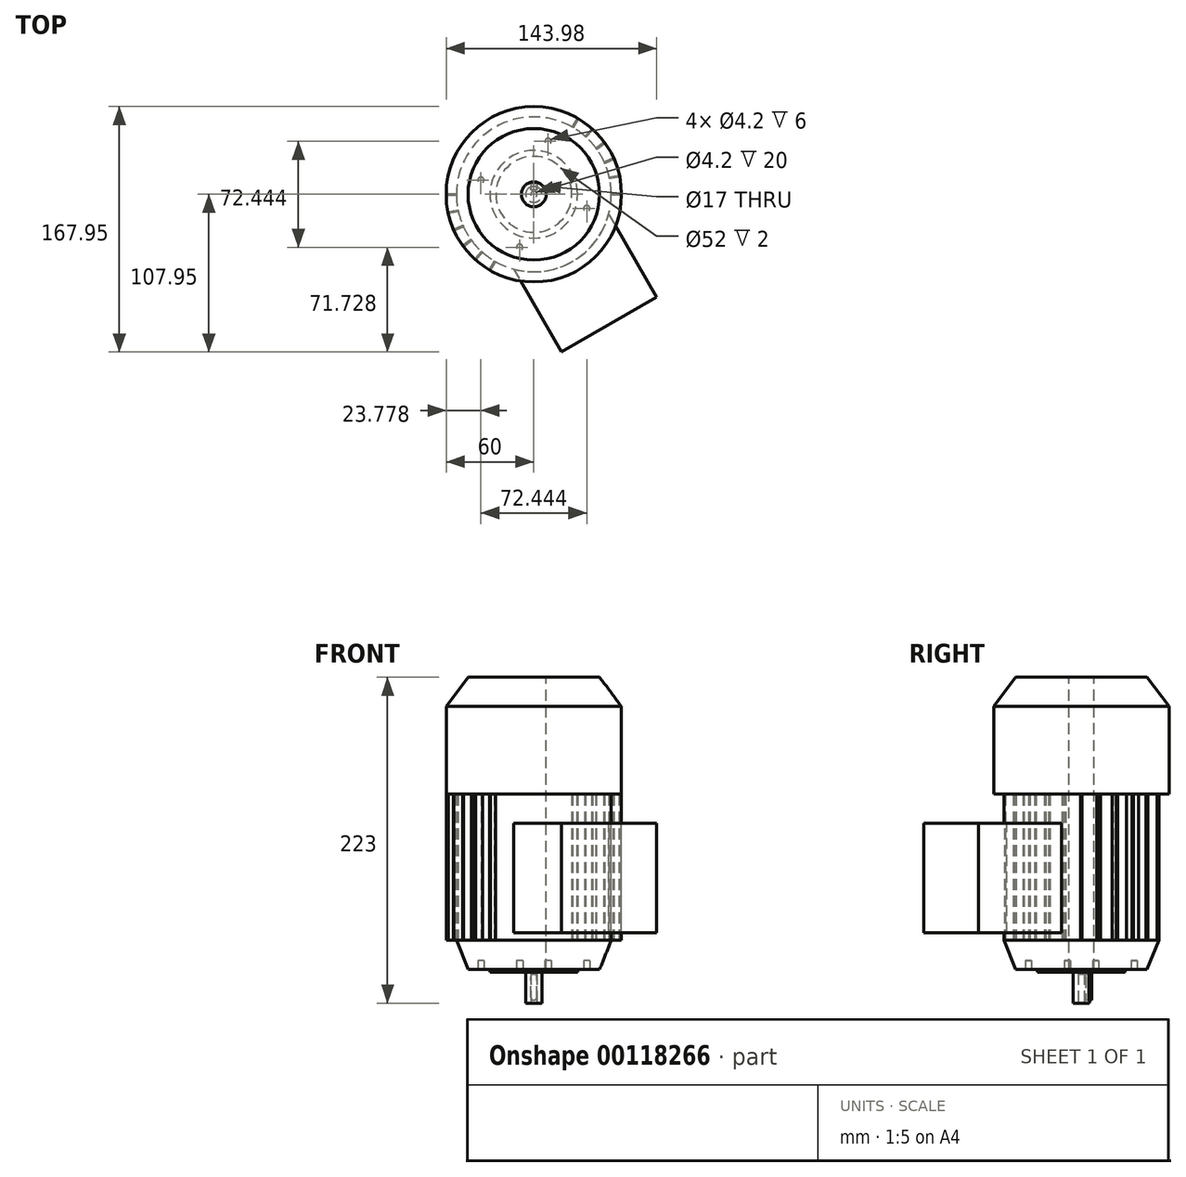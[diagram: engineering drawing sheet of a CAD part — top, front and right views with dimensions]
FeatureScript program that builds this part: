
annotation { "Feature Type Name" : "Feature", "Feature Type Description" : "" }
export const myFeature = defineFeature(function(context is Context, id is Id, definition is map)
    precondition{}
    {
        {
            var Q0;
            Q0=qCreatedBy(makeId("Front.planeOp"),FACE);
            var sketch = newSketch(context, id + "F0", { "sketchPlane" : qUnion([Q0])});
            skLineSegment(sketch, "E0", {"start": v(0, 200) * mm, "end": v(0, 0) * mm});
            skLineSegment(sketch, "E1", {"start": v(-8.5, 200) * mm, "end": v(-45, 200) * mm});
            skLineSegment(sketch, "E2", {"start": v(-45, 200) * mm, "end": v(-60, 180) * mm});
            skLineSegment(sketch, "E3", {"start": v(-53, 20) * mm, "end": v(-45, 0) * mm});
            skLineSegment(sketch, "E4", {"start": v(-45, 0) * mm, "end": v(-8.5, 0) * mm});
            skLineSegment(sketch, "E5", {"start": v(-60, 180) * mm, "end": v(-60, 120) * mm});
            skLineSegment(sketch, "E6", {"start": v(-60, 120) * mm, "end": v(-8.5, 120) * mm});
            skLineSegment(sketch, "E7", {"start": v(-53, 20) * mm, "end": v(0, 20) * mm});
            skLineSegment(sketch, "E8", {"start": v(-8.5, 200) * mm, "end": v(-8.5, 0) * mm});
            skPoint(sketch, "E9.orphan", {"position": v(0, 200) * mm});
            skLineSegment(sketch, "E10", {"start": v(-8.5, 200) * mm, "end": v(0, 200) * mm});
            skLineSegment(sketch, "E11", {"start": v(-8.5, 0) * mm, "end": v(0, 0) * mm});
            skLineSegment(sketch, "E12", {"start": v(-60, 20) * mm, "end": v(-53, 20) * mm});
            skLineSegment(sketch, "E13", {"start": v(-60, 120) * mm, "end": v(-60, 20) * mm});
            skPoint(sketch, "E14", {"position": v(-8.5, 120) * mm});
            skLineSegment(sketch, "E15", {"start": v(-8.5, 120) * mm, "end": v(0, 120) * mm});
            skLineSegment(sketch, "E16", {"start": v(-53, 20) * mm, "end": v(-53, 120) * mm});
            skLineSegment(sketch, "E17", {"start": v(-5.5, 0) * mm, "end": v(-5.5, -23) * mm});
            skLineSegment(sketch, "E18", {"start": v(-5.5, -23) * mm, "end": v(0, -23) * mm});
            skLineSegment(sketch, "E19", {"start": v(0, -23) * mm, "end": v(0, 0) * mm});
            skSolve(sketch);
        }
        {
            var Q0;
            {var subQ0=sQuery(id+"F0.wireOp",EDGE,"E3");Q0=makeQuery(id+"F0.imprint","IMPRINT",FACE,{"disambiguationData":[TD([[makeQuery(id+"F0.imprint","IMPRINT",EDGE,{"derivedFrom":subQ0}),1.0]])]});}
            var Q1;
            {var subQ4=sQuery(id+"F0.wireOp",EDGE,"E1");Q1=makeQuery(id+"F0.imprint","IMPRINT",FACE,{"disambiguationData":[TD([[makeQuery(id+"F0.imprint","IMPRINT",EDGE,{"derivedFrom":subQ4}),1.0]])]});}
            var Q2;
            {var subQ3=sQuery(id+"F0.wireOp",EDGE,"E16");Q2=makeQuery(id+"F0.imprint","IMPRINT",FACE,{"disambiguationData":[TD([[makeQuery(id+"F0.imprint","IMPRINT",EDGE,{"derivedFrom":subQ3}),-1.0]])]});}
            var Q3;
            {var subQ0=sQuery(id+"F0.wireOp",EDGE,"E3");Q3=makeQuery(id+"F0.imprint","IMPRINT",FACE,{"disambiguationData":[TD([[makeQuery(id+"F0.imprint","IMPRINT",EDGE,{"derivedFrom":subQ0}),1.0]])]});}
            var Q4;
            Q4=sQuery(id+"F0.wireOp",EDGE,"E0");
            revolve(context, id + "F1", {"entities" : qUnion([Q0, Q1, Q2, Q3]), "axis" : qUnion([Q4]), "revolveType" : RevolveType.FULL});
        }
        {
            var Q0;
            {var subQ0=sQuery(id+"F0.wireOp",EDGE,"E10");Q0=makeQuery(id+"F0.imprint","IMPRINT",FACE,{"disambiguationData":[TD([[makeQuery(id+"F0.imprint","IMPRINT",EDGE,{"derivedFrom":subQ0}),-1.0]])]});}
            var Q1;
            {var subQ3=sQuery(id+"F0.wireOp",EDGE,"E15");Q1=makeQuery(id+"F0.imprint","IMPRINT",FACE,{"disambiguationData":[TD([[makeQuery(id+"F0.imprint","IMPRINT",EDGE,{"derivedFrom":subQ3}),-1.0]])]});}
            var Q2;
            {var subQ3=sQuery(id+"F0.wireOp",EDGE,"E7");var subQ5=sQuery(id+"F0.wireOp",EDGE,"E0");var subQ6=makeQuery(id+"F0.imprint","INTERSECT",VERTEX,{"derivedFrom":[subQ5,subQ3]});Q2=makeQuery(id+"F0.imprint","IMPRINT",FACE,{"disambiguationData":[TD([[makeQuery(id+"F0.imprint","IMPRINT",EDGE,{"disambiguationData":[TD([[subQ6,1.0]])],"derivedFrom":subQ3}),-1.0]])]});}
            var Q3;
            {var subQ2=sQuery(id+"F0.wireOp",EDGE,"E17");Q3=makeQuery(id+"F0.imprint","IMPRINT",FACE,{"disambiguationData":[TD([[makeQuery(id+"F0.imprint","IMPRINT",EDGE,{"derivedFrom":subQ2}),1.0]])]});}
            var Q4;
            Q4=sQuery(id+"F0.wireOp",EDGE,"E0");
            revolve(context, id + "F2", {"entities" : qUnion([Q0, Q1, Q2, Q3]), "axis" : qUnion([Q4]), "revolveType" : RevolveType.FULL});
        }
        {
            var Q0;
            Q0=sQuery(id+"F0.wireOp",VERTEX,"E6.end");
            var Q1;
            Q1=sQuery(id+"F0.wireOp",EDGE,"E8");
            cPlane(context, id + "F3", {"entities" : qUnion([Q0, Q1]), "cplaneType" : CPlaneType.LINE_POINT, "offset" : 150 * mm, "width" : 150 * mm, "height" : 150 * mm});
        }
        {
            var Q0;
            Q0=qCreatedBy(id+"F3.planeOp",FACE);
            var sketch = newSketch(context, id + "F4", { "sketchPlane" : qUnion([Q0])});
            skLineSegment(sketch, "E20.0", {"start": v(-8.5, 0) * mm, "end": v(-45, 0) * mm});
            skLineSegment(sketch, "E20.1", {"start": v(-45, 0) * mm, "end": v(-60, 0) * mm});
            skLineSegment(sketch, "E21.0", {"start": v(-8.5, 0) * mm, "end": v(0, 0) * mm});
            skCircle(sketch, "E22", {"center": v(0, 0) * mm, "radius": 8.5 * mm});
            skCircle(sketch, "E23.0", {"center": v(0, 0) * mm, "radius": 53 * mm});
            skLineSegment(sketch, "E24", {"start": v(-60, 0) * mm, "end": v(-60, 0.5) * mm});
            skLineSegment(sketch, "E25", {"start": v(-60, 0.5) * mm, "end": v(-53, 0.5) * mm});
            skLineSegment(sketch, "E26", {"start": v(-53, 0.5) * mm, "end": v(-53, 0) * mm});
            skLineSegment(sketch, "E27.MirrorCS", {"start": v(-60, -0.5) * mm, "end": v(-53, -0.5) * mm});
            skLineSegment(sketch, "E28.MirrorCS", {"start": v(-60, 0) * mm, "end": v(-60, -0.5) * mm});
            skLineSegment(sketch, "E29.MirrorCS", {"start": v(-53, -0.5) * mm, "end": v(-53, 0) * mm});
            skLineSegment(sketch, "E30.1.0", {"start": v(-58.8, 11.99) * mm, "end": v(-51.94, 10.53) * mm});
            skLineSegment(sketch, "E30.1.1", {"start": v(-58.58, 12.96) * mm, "end": v(-51.74, 11.5) * mm});
            skLineSegment(sketch, "E30.1.2", {"start": v(-51.74, 11.5) * mm, "end": v(-51.84, 11.02) * mm});
            skLineSegment(sketch, "E30.1.3", {"start": v(-58.69, 12.47) * mm, "end": v(-58.8, 11.99) * mm});
            skLineSegment(sketch, "E30.1.4", {"start": v(-51.94, 10.53) * mm, "end": v(-51.84, 11.02) * mm});
            skLineSegment(sketch, "E30.1.5", {"start": v(-58.69, 12.47) * mm, "end": v(-58.58, 12.96) * mm});
            skLineSegment(sketch, "E30.2.0", {"start": v(-55.02, 23.95) * mm, "end": v(-48.62, 21.1) * mm});
            skLineSegment(sketch, "E30.2.1", {"start": v(-54.6, 24.86) * mm, "end": v(-48.21, 22.01) * mm});
            skLineSegment(sketch, "E30.2.2", {"start": v(-48.21, 22.01) * mm, "end": v(-48.42, 21.56) * mm});
            skLineSegment(sketch, "E30.2.3", {"start": v(-54.81, 24.4) * mm, "end": v(-55.02, 23.95) * mm});
            skLineSegment(sketch, "E30.2.4", {"start": v(-48.62, 21.1) * mm, "end": v(-48.42, 21.56) * mm});
            skLineSegment(sketch, "E30.2.5", {"start": v(-54.81, 24.4) * mm, "end": v(-54.6, 24.86) * mm});
            skLineSegment(sketch, "E30.3.0", {"start": v(-48.83, 34.86) * mm, "end": v(-43.17, 30.75) * mm});
            skLineSegment(sketch, "E30.3.1", {"start": v(-48.25, 35.67) * mm, "end": v(-42.58, 31.56) * mm});
            skLineSegment(sketch, "E30.3.2", {"start": v(-42.58, 31.56) * mm, "end": v(-42.88, 31.15) * mm});
            skLineSegment(sketch, "E30.3.3", {"start": v(-48.54, 35.27) * mm, "end": v(-48.83, 34.86) * mm});
            skLineSegment(sketch, "E30.3.4", {"start": v(-43.17, 30.75) * mm, "end": v(-42.88, 31.15) * mm});
            skLineSegment(sketch, "E30.3.5", {"start": v(-48.54, 35.27) * mm, "end": v(-48.25, 35.67) * mm});
            skLineSegment(sketch, "E30.4.0", {"start": v(-40.52, 44.25) * mm, "end": v(-35.83, 39.05) * mm});
            skLineSegment(sketch, "E30.4.1", {"start": v(-39.78, 44.92) * mm, "end": v(-35.1, 39.72) * mm});
            skLineSegment(sketch, "E30.4.2", {"start": v(-35.1, 39.72) * mm, "end": v(-35.46, 39.38) * mm});
            skLineSegment(sketch, "E30.4.3", {"start": v(-40.15, 44.59) * mm, "end": v(-40.52, 44.25) * mm});
            skLineSegment(sketch, "E30.4.4", {"start": v(-35.83, 39.05) * mm, "end": v(-35.46, 39.38) * mm});
            skLineSegment(sketch, "E30.4.5", {"start": v(-40.15, 44.59) * mm, "end": v(-39.78, 44.92) * mm});
            skLineSegment(sketch, "E30.5.0", {"start": v(-30.43, 51.71) * mm, "end": v(-26.93, 45.65) * mm});
            skLineSegment(sketch, "E30.5.1", {"start": v(-29.57, 52.21) * mm, "end": v(-26.07, 46.15) * mm});
            skLineSegment(sketch, "E30.5.2", {"start": v(-26.07, 46.15) * mm, "end": v(-26.5, 45.9) * mm});
            skLineSegment(sketch, "E30.5.3", {"start": v(-30, 51.96) * mm, "end": v(-30.43, 51.71) * mm});
            skLineSegment(sketch, "E30.5.4", {"start": v(-26.93, 45.65) * mm, "end": v(-26.5, 45.9) * mm});
            skLineSegment(sketch, "E30.5.5", {"start": v(-30, 51.96) * mm, "end": v(-29.57, 52.21) * mm});
            skLineSegment(sketch, "E30.anchor1", {"start": v(0, 0) * mm, "end": v(-60, -0.5) * mm, "construction": true});
            skLineSegment(sketch, "E30.anchor2", {"start": v(0, 0) * mm, "end": v(-30.43, 51.71) * mm, "construction": true});
            skLineSegment(sketch, "E31", {"start": v(-26.5, -45.9) * mm, "end": v(26.5, 45.9) * mm, "construction": true});
            skLineSegment(sketch, "E32.MirrorCS", {"start": v(30, -51.96) * mm, "end": v(30.43, -51.71) * mm});
            skLineSegment(sketch, "E33.MirrorCS", {"start": v(26.93, -45.65) * mm, "end": v(26.5, -45.9) * mm});
            skLineSegment(sketch, "E34.MirrorCS", {"start": v(30.43, -51.71) * mm, "end": v(26.93, -45.65) * mm});
            skLineSegment(sketch, "E35.MirrorCS", {"start": v(29.57, -52.21) * mm, "end": v(26.07, -46.15) * mm});
            skLineSegment(sketch, "E36.MirrorCS", {"start": v(54.81, -24.4) * mm, "end": v(54.6, -24.86) * mm});
            skLineSegment(sketch, "E37.MirrorCS", {"start": v(43.17, -30.75) * mm, "end": v(42.88, -31.15) * mm});
            skLineSegment(sketch, "E38.MirrorCS", {"start": v(51.94, -10.53) * mm, "end": v(51.84, -11.02) * mm});
            skLineSegment(sketch, "E39.MirrorCS", {"start": v(40.15, -44.59) * mm, "end": v(40.52, -44.25) * mm});
            skLineSegment(sketch, "E40.MirrorCS", {"start": v(58.8, -11.99) * mm, "end": v(51.94, -10.53) * mm});
            skLineSegment(sketch, "E41.MirrorCS", {"start": v(39.78, -44.92) * mm, "end": v(35.1, -39.72) * mm});
            skLineSegment(sketch, "E42.MirrorCS", {"start": v(40.52, -44.25) * mm, "end": v(35.83, -39.05) * mm});
            skLineSegment(sketch, "E43.MirrorCS", {"start": v(53, -0.5) * mm, "end": v(53, 0) * mm});
            skLineSegment(sketch, "E44.MirrorCS", {"start": v(54.6, -24.86) * mm, "end": v(48.21, -22.01) * mm});
            skLineSegment(sketch, "E45.MirrorCS", {"start": v(60, 0.5) * mm, "end": v(53, 0.5) * mm});
            skLineSegment(sketch, "E46.MirrorCS", {"start": v(58.58, -12.96) * mm, "end": v(51.74, -11.5) * mm});
            skLineSegment(sketch, "E47.MirrorCS", {"start": v(60, -0.5) * mm, "end": v(53, -0.5) * mm});
            skLineSegment(sketch, "E48.MirrorCS", {"start": v(58.69, -12.47) * mm, "end": v(58.58, -12.96) * mm});
            skLineSegment(sketch, "E49.MirrorCS", {"start": v(48.21, -22.01) * mm, "end": v(48.42, -21.56) * mm});
            skLineSegment(sketch, "E50.MirrorCS", {"start": v(40.15, -44.59) * mm, "end": v(39.78, -44.92) * mm});
            skLineSegment(sketch, "E51.MirrorCS", {"start": v(35.83, -39.05) * mm, "end": v(35.46, -39.38) * mm});
            skLineSegment(sketch, "E52.MirrorCS", {"start": v(55.02, -23.95) * mm, "end": v(48.62, -21.1) * mm});
            skLineSegment(sketch, "E53.MirrorCS", {"start": v(60, 0) * mm, "end": v(60, -0.5) * mm});
            skLineSegment(sketch, "E54.MirrorCS", {"start": v(26.5, -45.9) * mm, "end": v(26.5, -45.9) * mm});
            skLineSegment(sketch, "E55.MirrorCS", {"start": v(48.83, -34.86) * mm, "end": v(43.17, -30.75) * mm});
            skLineSegment(sketch, "E56.MirrorCS", {"start": v(48.25, -35.67) * mm, "end": v(42.58, -31.56) * mm});
            skLineSegment(sketch, "E57.MirrorCS", {"start": v(48.54, -35.27) * mm, "end": v(48.83, -34.86) * mm});
            skLineSegment(sketch, "E58", {"start": v(54.81, -24.4) * mm, "end": v(55.02, -23.95) * mm});
            skLineSegment(sketch, "E59", {"start": v(48.25, -35.67) * mm, "end": v(48.54, -35.27) * mm});
            skLineSegment(sketch, "E60", {"start": v(29.57, -52.21) * mm, "end": v(30, -51.96) * mm});
            skLineSegment(sketch, "E61", {"start": v(35.1, -39.72) * mm, "end": v(35.46, -39.38) * mm});
            skLineSegment(sketch, "E62", {"start": v(60, 0) * mm, "end": v(60, 0.5) * mm});
            skLineSegment(sketch, "E63", {"start": v(58.69, -12.47) * mm, "end": v(58.8, -11.99) * mm});
            skSolve(sketch);
        }
        {
            var Q0;
            {var subQ2=sQuery(id+"F4.wireOp",EDGE,"E30.1.2");Q0=makeQuery(id+"F4.imprint","IMPRINT",FACE,{"disambiguationData":[TD([[makeQuery(id+"F4.imprint","IMPRINT",EDGE,{"derivedFrom":subQ2}),-1.0]])]});}
            var Q1;
            {var subQ1=sQuery(id+"F4.wireOp",EDGE,"E30.1.0");Q1=makeQuery(id+"F4.imprint","IMPRINT",FACE,{"disambiguationData":[TD([[makeQuery(id+"F4.imprint","IMPRINT",EDGE,{"derivedFrom":subQ1}),1.0]])]});}
            var Q2;
            {var subQ1=sQuery(id+"F4.wireOp",EDGE,"E30.3.0");Q2=makeQuery(id+"F4.imprint","IMPRINT",FACE,{"disambiguationData":[TD([[makeQuery(id+"F4.imprint","IMPRINT",EDGE,{"derivedFrom":subQ1}),1.0]])]});}
            var Q3;
            {var subQ1=sQuery(id+"F4.wireOp",EDGE,"E30.4.0");Q3=makeQuery(id+"F4.imprint","IMPRINT",FACE,{"disambiguationData":[TD([[makeQuery(id+"F4.imprint","IMPRINT",EDGE,{"derivedFrom":subQ1}),1.0]])]});}
            var Q4;
            {var subQ1=sQuery(id+"F4.wireOp",EDGE,"E30.5.0");Q4=makeQuery(id+"F4.imprint","IMPRINT",FACE,{"disambiguationData":[TD([[makeQuery(id+"F4.imprint","IMPRINT",EDGE,{"derivedFrom":subQ1}),1.0]])]});}
            var Q5;
            {var subQ2=sQuery(id+"F4.wireOp",EDGE,"E30.2.2");Q5=makeQuery(id+"F4.imprint","IMPRINT",FACE,{"disambiguationData":[TD([[makeQuery(id+"F4.imprint","IMPRINT",EDGE,{"derivedFrom":subQ2}),-1.0]])]});}
            var Q6;
            {var subQ2=sQuery(id+"F4.wireOp",EDGE,"E30.3.2");Q6=makeQuery(id+"F4.imprint","IMPRINT",FACE,{"disambiguationData":[TD([[makeQuery(id+"F4.imprint","IMPRINT",EDGE,{"derivedFrom":subQ2}),-1.0]])]});}
            var Q7;
            {var subQ2=sQuery(id+"F4.wireOp",EDGE,"E30.4.2");Q7=makeQuery(id+"F4.imprint","IMPRINT",FACE,{"disambiguationData":[TD([[makeQuery(id+"F4.imprint","IMPRINT",EDGE,{"derivedFrom":subQ2}),-1.0]])]});}
            var Q8;
            {var subQ2=sQuery(id+"F4.wireOp",EDGE,"E30.5.2");Q8=makeQuery(id+"F4.imprint","IMPRINT",FACE,{"disambiguationData":[TD([[makeQuery(id+"F4.imprint","IMPRINT",EDGE,{"derivedFrom":subQ2}),-1.0]])]});}
            var Q9;
            {var subQ1=sQuery(id+"F4.wireOp",EDGE,"E30.2.0");Q9=makeQuery(id+"F4.imprint","IMPRINT",FACE,{"disambiguationData":[TD([[makeQuery(id+"F4.imprint","IMPRINT",EDGE,{"derivedFrom":subQ1}),1.0]])]});}
            var Q10;
            {var subQ0=sQuery(id+"F4.wireOp",EDGE,"E24");Q10=makeQuery(id+"F4.imprint","IMPRINT",FACE,{"disambiguationData":[TD([[makeQuery(id+"F4.imprint","IMPRINT",EDGE,{"derivedFrom":subQ0}),-1.0]])]});}
            var Q11;
            Q11=makeQuery(id+"F4.imprint","IMPRINT",FACE,{"disambiguationData":[TD([[makeQuery(id+"F4.imprint","IMPRINT",EDGE,{"derivedFrom":sQuery(id+"F4.wireOp",EDGE,"E39.MirrorCS")}),1.0]])]});
            var Q12;
            {var subQ4=sQuery(id+"F4.wireOp",EDGE,"E32.MirrorCS");Q12=makeQuery(id+"F4.imprint","IMPRINT",FACE,{"disambiguationData":[TD([[makeQuery(id+"F4.imprint","IMPRINT",EDGE,{"derivedFrom":subQ4}),1.0]])]});}
            var Q13;
            {var subQ1=sQuery(id+"F4.wireOp",EDGE,"E55.MirrorCS");Q13=makeQuery(id+"F4.imprint","IMPRINT",FACE,{"disambiguationData":[TD([[makeQuery(id+"F4.imprint","IMPRINT",EDGE,{"derivedFrom":subQ1}),1.0]])]});}
            var Q14;
            Q14=makeQuery(id+"F4.imprint","IMPRINT",FACE,{"disambiguationData":[TD([[makeQuery(id+"F4.imprint","IMPRINT",EDGE,{"derivedFrom":sQuery(id+"F4.wireOp",EDGE,"E36.MirrorCS")}),-1.0]])]});
            var Q15;
            {var subQ1=sQuery(id+"F4.wireOp",EDGE,"E40.MirrorCS");Q15=makeQuery(id+"F4.imprint","IMPRINT",FACE,{"disambiguationData":[TD([[makeQuery(id+"F4.imprint","IMPRINT",EDGE,{"derivedFrom":subQ1}),1.0]])]});}
            var Q16;
            {var subQ1=sQuery(id+"F4.wireOp",EDGE,"E45.MirrorCS");Q16=makeQuery(id+"F4.imprint","IMPRINT",FACE,{"disambiguationData":[TD([[makeQuery(id+"F4.imprint","IMPRINT",EDGE,{"derivedFrom":subQ1}),1.0]])]});}
            extrude(context, id + "F5", {"entities" : qUnion([Q0, Q1, Q2, Q3, Q4, Q5, Q6, Q7, Q8, Q9, Q10, Q11, Q12, Q13, Q14, Q15, Q16]), "operationType" : NewBodyOperationType.ADD, "depth" : 100 * mm});
        }
        {
            var Q0;
            Q0=qCreatedBy(makeId("Top.planeOp"),FACE);
            var sketch = newSketch(context, id + "F6", { "sketchPlane" : qUnion([Q0])});
            skCircle(sketch, "E64.0", {"center": v(0, 0) * mm, "radius": 45 * mm, "construction": true});
            skCircle(sketch, "E65", {"center": v(0, 0) * mm, "radius": 37.5 * mm, "construction": true});
            skLineSegment(sketch, "E66.0", {"start": v(-26.5, 45.9) * mm, "end": v(26.5, -45.9) * mm, "construction": true});
            skLineSegment(sketch, "E67", {"start": v(-32.48, -18.75) * mm, "end": v(32.48, 18.75) * mm, "construction": true});
            skLineSegment(sketch, "E68", {"start": v(32.48, 18.75) * mm, "end": v(38.97, 22.5) * mm, "construction": true});
            skLineSegment(sketch, "E69", {"start": v(-32.48, -18.75) * mm, "end": v(-38.97, -22.5) * mm, "construction": true});
            skLineSegment(sketch, "E70", {"start": v(0, 0) * mm, "end": v(43.47, -11.65) * mm, "construction": true});
            skLineSegment(sketch, "E71", {"start": v(0, 0) * mm, "end": v(-36.22, 9.7) * mm, "construction": true});
            skLineSegment(sketch, "E72", {"start": v(-9.7, -36.22) * mm, "end": v(9.7, 36.22) * mm, "construction": true});
            skCircle(sketch, "E73", {"center": v(36.22, -9.7) * mm, "radius": 2.1 * mm});
            skCircle(sketch, "E74.1.0", {"center": v(9.7, 36.22) * mm, "radius": 2.1 * mm});
            skCircle(sketch, "E74.2.0", {"center": v(-36.22, 9.7) * mm, "radius": 2.1 * mm});
            skCircle(sketch, "E74.3.0", {"center": v(-9.7, -36.22) * mm, "radius": 2.1 * mm});
            skCircle(sketch, "E75", {"center": v(0, 0) * mm, "radius": 30 * mm});
            skCircle(sketch, "E76", {"center": v(0, 0) * mm, "radius": 26 * mm});
            skSolve(sketch);
        }
        {
            var Q0;
            Q0=makeQuery(id+"F6.imprint","IMPRINT",FACE,{"disambiguationData":[TD([[makeQuery(id+"F6.imprint","IMPRINT",EDGE,{"derivedFrom":sQuery(id+"F6.wireOp",EDGE,"E73")}),1.0]])]});
            var Q1;
            Q1=makeQuery(id+"F6.imprint","IMPRINT",FACE,{"disambiguationData":[TD([[makeQuery(id+"F6.imprint","IMPRINT",EDGE,{"derivedFrom":sQuery(id+"F6.wireOp",EDGE,"E74.1.0")}),1.0]])]});
            var Q2;
            Q2=makeQuery(id+"F6.imprint","IMPRINT",FACE,{"disambiguationData":[TD([[makeQuery(id+"F6.imprint","IMPRINT",EDGE,{"derivedFrom":sQuery(id+"F6.wireOp",EDGE,"E74.3.0")}),1.0]])]});
            var Q3;
            Q3=makeQuery(id+"F6.imprint","IMPRINT",FACE,{"disambiguationData":[TD([[makeQuery(id+"F6.imprint","IMPRINT",EDGE,{"derivedFrom":sQuery(id+"F6.wireOp",EDGE,"E74.2.0")}),1.0]])]});
            var Q4;
            Q4=makeQuery(id+"F6.imprint","IMPRINT",FACE,{"disambiguationData":[TD([[makeQuery(id+"F6.imprint","IMPRINT",EDGE,{"derivedFrom":sQuery(id+"F6.wireOp",EDGE,"E73")}),1.0]])]});
            var Q5;
            Q5=makeQuery(id+"F6.imprint","IMPRINT",FACE,{"disambiguationData":[TD([[makeQuery(id+"F6.imprint","IMPRINT",EDGE,{"derivedFrom":sQuery(id+"F6.wireOp",EDGE,"E74.3.0")}),1.0]])]});
            var Q6;
            Q6=makeQuery(id+"F6.imprint","IMPRINT",FACE,{"disambiguationData":[TD([[makeQuery(id+"F6.imprint","IMPRINT",EDGE,{"derivedFrom":sQuery(id+"F6.wireOp",EDGE,"E74.2.0")}),1.0]])]});
            var Q7;
            Q7=makeQuery(id+"F6.imprint","IMPRINT",FACE,{"disambiguationData":[TD([[makeQuery(id+"F6.imprint","IMPRINT",EDGE,{"derivedFrom":sQuery(id+"F6.wireOp",EDGE,"E74.1.0")}),1.0]])]});
            extrude(context, id + "F7", {"entities" : qUnion([Q0, Q1, Q2, Q3, Q4, Q5, Q6, Q7]), "operationType" : NewBodyOperationType.REMOVE, "depth" : 6 * mm});
        }
        {
            var Q0;
            Q0=sQuery(id+"F6.wireOp",EDGE,"E66.0");
            var Q1;
            Q1=sQuery(id+"F6.wireOp",VERTEX,"E66.0.end");
            cPlane(context, id + "F8", {"entities" : qUnion([Q0, Q1]), "cplaneType" : CPlaneType.LINE_POINT, "offset" : 150 * mm, "width" : 150 * mm, "height" : 150 * mm});
        }
        {
            var Q0;
            Q0=qCreatedBy(id+"F8.planeOp",FACE);
            var sketch = newSketch(context, id + "F9", { "sketchPlane" : qUnion([Q0])});
            skLineSegment(sketch, "E77.0", {"start": v(0, 200) * mm, "end": v(0, 0) * mm, "construction": true});
            skLineSegment(sketch, "E78.0", {"start": v(-37.5, 0) * mm, "end": v(37.5, 0) * mm, "construction": true});
            skLineSegment(sketch, "E79.0", {"start": v(-51.7, 120) * mm, "end": v(51.7, 120) * mm, "construction": true});
            skPoint(sketch, "E80", {"position": v(0, 120) * mm});
            skLineSegment(sketch, "E81", {"start": v(0, 120) * mm, "end": v(0, 100) * mm});
            skLineSegment(sketch, "E82", {"start": v(37.5, 100) * mm, "end": v(-37.5, 100) * mm});
            skLineSegment(sketch, "E83", {"start": v(-37.5, 100) * mm, "end": v(-37.5, 25) * mm});
            skLineSegment(sketch, "E84", {"start": v(-37.5, 25) * mm, "end": v(37.5, 25) * mm});
            skLineSegment(sketch, "E85", {"start": v(37.5, 25) * mm, "end": v(37.5, 100) * mm});
            skPoint(sketch, "E86", {"position": v(0, 100) * mm});
            skSolve(sketch);
        }
        {
            var Q0;
            {var subQ0=sQuery(id+"F9.wireOp",EDGE,"E83");Q0=makeQuery(id+"F9.imprint","IMPRINT",FACE,{"disambiguationData":[TD([[makeQuery(id+"F9.imprint","IMPRINT",EDGE,{"derivedFrom":subQ0}),1.0]])]});}
            var Q1;
            Q1=makeQuery(id+"F1.opRevolve","SWEPT_BODY",BODY,{"disambiguationData":[OSD([sQuery(id+"F0.wireOp",EDGE,"E1"),sQuery(id+"F0.wireOp",EDGE,"E2"),sQuery(id+"F0.wireOp",EDGE,"E3"),sQuery(id+"F0.wireOp",EDGE,"E4"),sQuery(id+"F0.wireOp",EDGE,"E5"),sQuery(id+"F0.wireOp",EDGE,"E6"),sQuery(id+"F0.wireOp",EDGE,"E8"),sQuery(id+"F0.wireOp",EDGE,"E16")])]});
            extrude(context, id + "F10", {"entities" : qUnion([Q0]), "operationType" : NewBodyOperationType.ADD, "endBound" : BoundingType.UP_TO_BODY, "oppositeDirection" : true, "endBoundEntityBody" : qUnion([Q1]), "depth" : 25 * mm, "hasSecondDirection" : true, "secondDirectionOppositeDirection" : false, "secondDirectionDepth" : 50 * mm});
        }
        {
            var Q0;
            Q0=qCreatedBy(makeId("Front.planeOp"),FACE);
            cPlane(context, id + "F11", {"entities" : qUnion([Q0]), "cplaneType" : CPlaneType.OFFSET, "offset" : 5.5 * mm, "oppositeDirection" : true, "width" : 150 * mm, "height" : 150 * mm});
        }
        {
            var Q0;
            Q0=qCreatedBy(id+"F11.planeOp",FACE);
            var sketch = newSketch(context, id + "F12", { "sketchPlane" : qUnion([Q0])});
            skLineSegment(sketch, "E87", {"start": v(0, -23) * mm, "end": v(0, 0) * mm, "construction": true});
            skCircle(sketch, "E88", {"center": v(0, -5) * mm, "radius": 2 * mm});
            skCircle(sketch, "E89", {"center": v(0, -19) * mm, "radius": 2 * mm});
            skLineSegment(sketch, "E90", {"start": v(-2, -5) * mm, "end": v(-2, -19) * mm});
            skLineSegment(sketch, "E91", {"start": v(2, -5) * mm, "end": v(2, -19) * mm});
            skLineSegment(sketch, "E92.0", {"start": v(-5.5, -23) * mm, "end": v(5.5, -23) * mm});
            skSolve(sketch);
        }
        {
            var Q0;
            {var subQ0=sQuery(id+"F12.wireOp",EDGE,"E90");Q0=makeQuery(id+"F12.imprint","IMPRINT",FACE,{"disambiguationData":[TD([[makeQuery(id+"F12.imprint","IMPRINT",EDGE,{"derivedFrom":subQ0}),1.0]])]});}
            var Q1;
            {var subQ0=sQuery(id+"F12.wireOp",EDGE,"E88");var subQ1=makeQuery(id+"F12.imprint","INTERSECT",VERTEX,{"derivedFrom":[subQ0,sQuery(id+"F12.wireOp",EDGE,"E90")]});Q1=makeQuery(id+"F12.imprint","IMPRINT",FACE,{"disambiguationData":[TD([[makeQuery(id+"F12.imprint","IMPRINT",EDGE,{"disambiguationData":[TD([[subQ1,1.0]])],"derivedFrom":subQ0}),1.0]])]});}
            var Q2;
            {var subQ0=sQuery(id+"F12.wireOp",EDGE,"E89");var subQ1=makeQuery(id+"F12.imprint","INTERSECT",VERTEX,{"derivedFrom":[subQ0,sQuery(id+"F12.wireOp",EDGE,"E90")]});Q2=makeQuery(id+"F12.imprint","IMPRINT",FACE,{"disambiguationData":[TD([[makeQuery(id+"F12.imprint","IMPRINT",EDGE,{"disambiguationData":[TD([[subQ1,1.0]])],"derivedFrom":subQ0}),1.0]])]});}
            extrude(context, id + "F13", {"entities" : qUnion([Q0, Q1, Q2]), "operationType" : NewBodyOperationType.REMOVE, "depth" : 2.5 * mm});
        }
        {
            var Q0;
            Q0=makeQuery(id+"F6.imprint","IMPRINT",FACE,{"disambiguationData":[TD([[makeQuery(id+"F6.imprint","IMPRINT",EDGE,{"derivedFrom":sQuery(id+"F6.wireOp",EDGE,"E75")}),1.0]])]});
            extrude(context, id + "F14", {"entities" : qUnion([Q0]), "operationType" : NewBodyOperationType.ADD, "oppositeDirection" : true, "depth" : 2 * mm});
        }
        {
            var Q0;
            {var subQ0=sQuery(id+"F12.wireOp",EDGE,"E90");Q0=makeQuery(id+"F12.imprint","IMPRINT",FACE,{"disambiguationData":[TD([[makeQuery(id+"F12.imprint","IMPRINT",EDGE,{"derivedFrom":subQ0}),1.0]])]});}
            var Q1;
            {var subQ0=sQuery(id+"F12.wireOp",EDGE,"E88");var subQ1=makeQuery(id+"F12.imprint","INTERSECT",VERTEX,{"derivedFrom":[subQ0,sQuery(id+"F12.wireOp",EDGE,"E90")]});Q1=makeQuery(id+"F12.imprint","IMPRINT",FACE,{"disambiguationData":[TD([[makeQuery(id+"F12.imprint","IMPRINT",EDGE,{"disambiguationData":[TD([[subQ1,1.0]])],"derivedFrom":subQ0}),1.0]])]});}
            var Q2;
            {var subQ0=sQuery(id+"F12.wireOp",EDGE,"E89");var subQ1=makeQuery(id+"F12.imprint","INTERSECT",VERTEX,{"derivedFrom":[subQ0,sQuery(id+"F12.wireOp",EDGE,"E90")]});Q2=makeQuery(id+"F12.imprint","IMPRINT",FACE,{"disambiguationData":[TD([[makeQuery(id+"F12.imprint","IMPRINT",EDGE,{"disambiguationData":[TD([[subQ1,1.0]])],"derivedFrom":subQ0}),1.0]])]});}
            extrude(context, id + "F15", {"entities" : qUnion([Q0, Q1, Q2]), "oppositeDirection" : true, "depth" : 1.5 * mm, "hasSecondDirection" : true, "secondDirectionOppositeDirection" : false, "secondDirectionDepth" : 2.5 * mm});
        }
        {
            var Q0;
            Q0=makeQuery(id+"F2.opRevolve","SWEPT_FACE",FACE,{"disambiguationData":[OSD([sQuery(id+"F0.wireOp",EDGE,"E18")])]});
            var sketch = newSketch(context, id + "F16", { "sketchPlane" : qUnion([Q0])});
            skCircle(sketch, "E93.0", {"center": v(0, 0) * mm, "radius": 5.5 * mm});
            skCircle(sketch, "E94", {"center": v(0, 0) * mm, "radius": 2.1 * mm});
            skSolve(sketch);
        }
        {
            var Q0;
            Q0=makeQuery(id+"F16.imprint","IMPRINT",FACE,{"disambiguationData":[TD([[makeQuery(id+"F16.imprint","IMPRINT",EDGE,{"derivedFrom":sQuery(id+"F16.wireOp",EDGE,"E94")}),1.0]])]});
            extrude(context, id + "F17", {"entities" : qUnion([Q0]), "operationType" : NewBodyOperationType.REMOVE, "oppositeDirection" : true, "depth" : 20 * mm});
        }
    });
